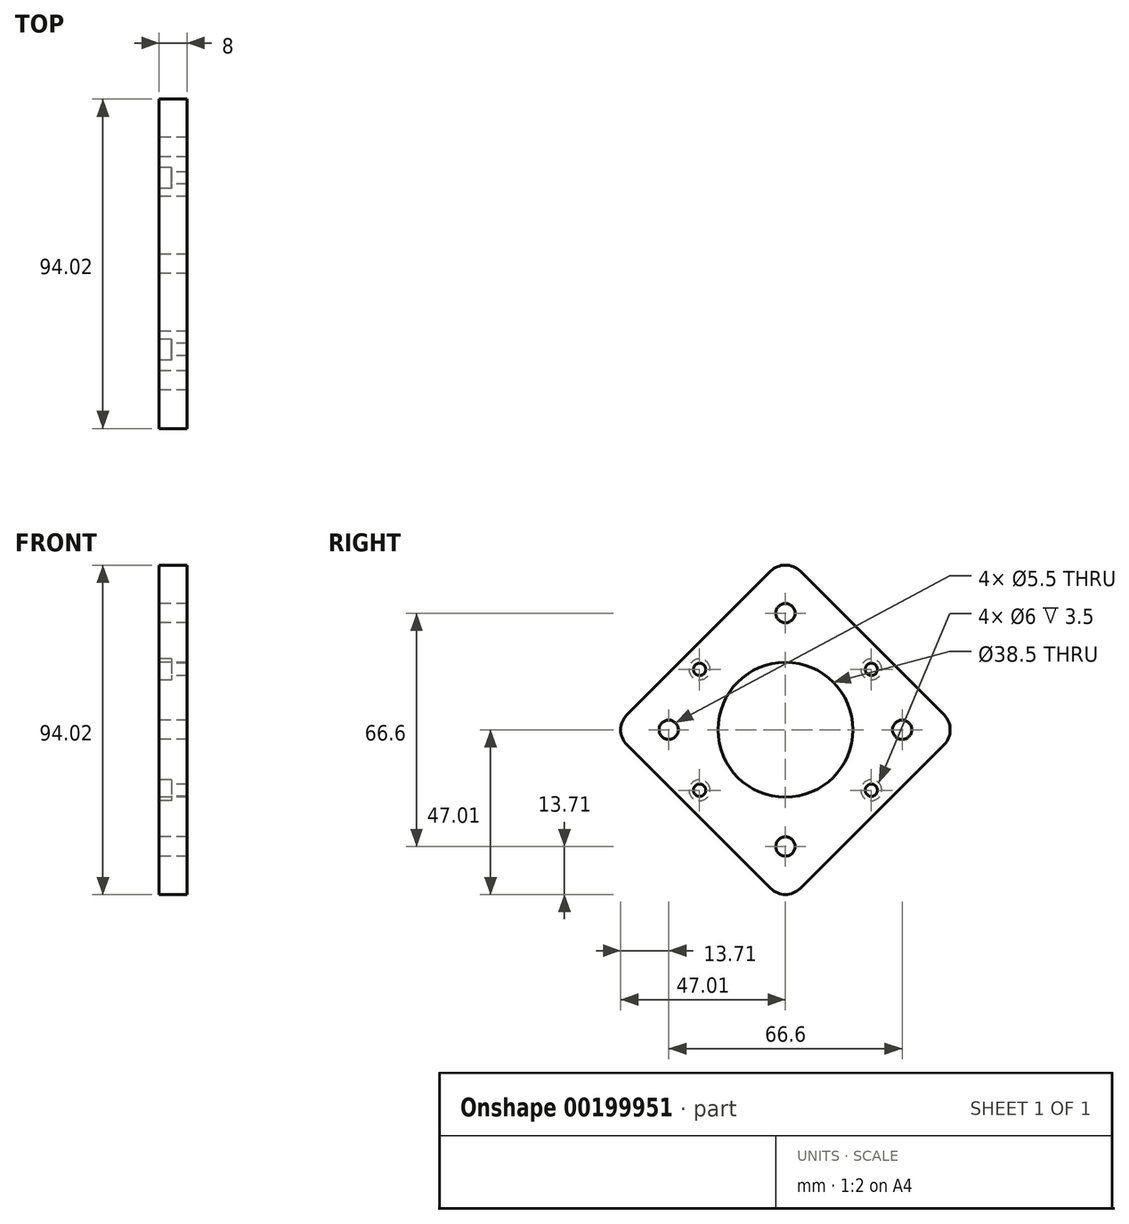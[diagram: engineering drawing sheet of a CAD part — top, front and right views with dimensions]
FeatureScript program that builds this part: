
annotation { "Feature Type Name" : "Feature", "Feature Type Description" : "" }
export const myFeature = defineFeature(function(context is Context, id is Id, definition is map)
    precondition{}
    {
        {
            var Q0;
            Q0=qCreatedBy(makeId("Right.planeOp"),FACE);
            var sketch = newSketch(context, id + "F0", { "sketchPlane" : qUnion([Q0])});
            skLineSegment(sketch, "E0", {"start": v(-4.24, 45.25) * mm, "end": v(-45.25, 4.24) * mm});
            skLineSegment(sketch, "E1", {"start": v(-45.25, -4.24) * mm, "end": v(-4.24, -45.25) * mm});
            skLineSegment(sketch, "E2", {"start": v(4.24, -45.25) * mm, "end": v(45.25, -4.24) * mm});
            skLineSegment(sketch, "E3", {"start": v(45.25, 4.24) * mm, "end": v(4.24, 45.25) * mm});
            skPoint(sketch, "E4.visualSharp", {"position": v(0, 49.5) * mm});
            skArc(sketch, "E4.filletArc", {"start": v(4.24, 45.25) * mm, "mid": v(0, 47.01) * mm, "end": v(-4.24, 45.25) * mm});
            skPoint(sketch, "E5.visualSharp", {"position": v(-49.5, 0) * mm});
            skArc(sketch, "E5.filletArc", {"start": v(-45.25, 4.24) * mm, "mid": v(-47.01, 0) * mm, "end": v(-45.25, -4.24) * mm});
            skPoint(sketch, "E6.visualSharp", {"position": v(0, -49.5) * mm});
            skArc(sketch, "E6.filletArc", {"start": v(-4.24, -45.25) * mm, "mid": v(0, -47.01) * mm, "end": v(4.24, -45.25) * mm});
            skPoint(sketch, "E7.visualSharp", {"position": v(49.5, 0) * mm});
            skArc(sketch, "E7.filletArc", {"start": v(45.25, -4.24) * mm, "mid": v(47.01, 0) * mm, "end": v(45.25, 4.24) * mm});
            skCircle(sketch, "E8", {"center": v(0, 33.3) * mm, "radius": 2.75 * mm});
            skCircle(sketch, "E9", {"center": v(-33.3, 0) * mm, "radius": 2.75 * mm});
            skCircle(sketch, "E10", {"center": v(0, -33.3) * mm, "radius": 2.75 * mm});
            skCircle(sketch, "E11", {"center": v(33.3, 0) * mm, "radius": 2.75 * mm});
            skLineSegment(sketch, "E12.bottom", {"start": v(24.5, 17.25) * mm, "end": v(-24.5, 17.25) * mm, "construction": true});
            skLineSegment(sketch, "E12.top", {"start": v(24.5, -17.25) * mm, "end": v(-24.5, -17.25) * mm, "construction": true});
            skLineSegment(sketch, "E12.left", {"start": v(24.5, 17.25) * mm, "end": v(24.5, -17.25) * mm, "construction": true});
            skLineSegment(sketch, "E12.right", {"start": v(-24.5, 17.25) * mm, "end": v(-24.5, -17.25) * mm, "construction": true});
            skPoint(sketch, "E12.middle", {"position": v(0, 0) * mm});
            skCircle(sketch, "E13", {"center": v(-24.5, 17.25) * mm, "radius": 1.75 * mm});
            skCircle(sketch, "E14", {"center": v(24.5, 17.25) * mm, "radius": 1.75 * mm});
            skCircle(sketch, "E15", {"center": v(24.5, -17.25) * mm, "radius": 1.75 * mm});
            skCircle(sketch, "E16", {"center": v(-24.5, -17.25) * mm, "radius": 1.75 * mm});
            skCircle(sketch, "E17", {"center": v(0, 0) * mm, "radius": 19.25 * mm});
            skSolve(sketch);
        }
        {
            var Q0;
            Q0 = qSketchRegion(id + "F0", true);
            extrude(context, id + "F1", {"entities" : qUnion([Q0]), "depth" : 8 * mm});
        }
        {
            var Q0;
            Q0=makeQuery(id+"F1.opExtrude","CAP_FACE",FACE,{"disambiguationData":[OSD([sQuery(id+"F0.wireOp",EDGE,"E0"),sQuery(id+"F0.wireOp",EDGE,"E1"),sQuery(id+"F0.wireOp",EDGE,"E2"),sQuery(id+"F0.wireOp",EDGE,"E3"),sQuery(id+"F0.wireOp",EDGE,"E4.filletArc"),sQuery(id+"F0.wireOp",EDGE,"E5.filletArc"),sQuery(id+"F0.wireOp",EDGE,"E6.filletArc"),sQuery(id+"F0.wireOp",EDGE,"E7.filletArc"),sQuery(id+"F0.wireOp",EDGE,"E8"),sQuery(id+"F0.wireOp",EDGE,"E9"),sQuery(id+"F0.wireOp",EDGE,"E10"),sQuery(id+"F0.wireOp",EDGE,"E11"),sQuery(id+"F0.wireOp",EDGE,"E13"),sQuery(id+"F0.wireOp",EDGE,"E14"),sQuery(id+"F0.wireOp",EDGE,"E15"),sQuery(id+"F0.wireOp",EDGE,"E16"),sQuery(id+"F0.wireOp",EDGE,"E17")])],"isStart":true});
            var sketch = newSketch(context, id + "F2", { "sketchPlane" : qUnion([Q0])});
            skCircle(sketch, "E18", {"center": v(24.5, 17.25) * mm, "radius": 3 * mm});
            skCircle(sketch, "E19", {"center": v(-24.5, 17.25) * mm, "radius": 3 * mm});
            skCircle(sketch, "E20", {"center": v(-24.5, -17.25) * mm, "radius": 3 * mm});
            skCircle(sketch, "E21", {"center": v(24.5, -17.25) * mm, "radius": 3 * mm});
            skSolve(sketch);
        }
        {
            var Q0;
            Q0 = qSketchRegion(id + "F2", true);
            extrude(context, id + "F3", {"entities" : qUnion([Q0]), "operationType" : NewBodyOperationType.REMOVE, "oppositeDirection" : true, "depth" : 3.5 * mm});
        }
    });
